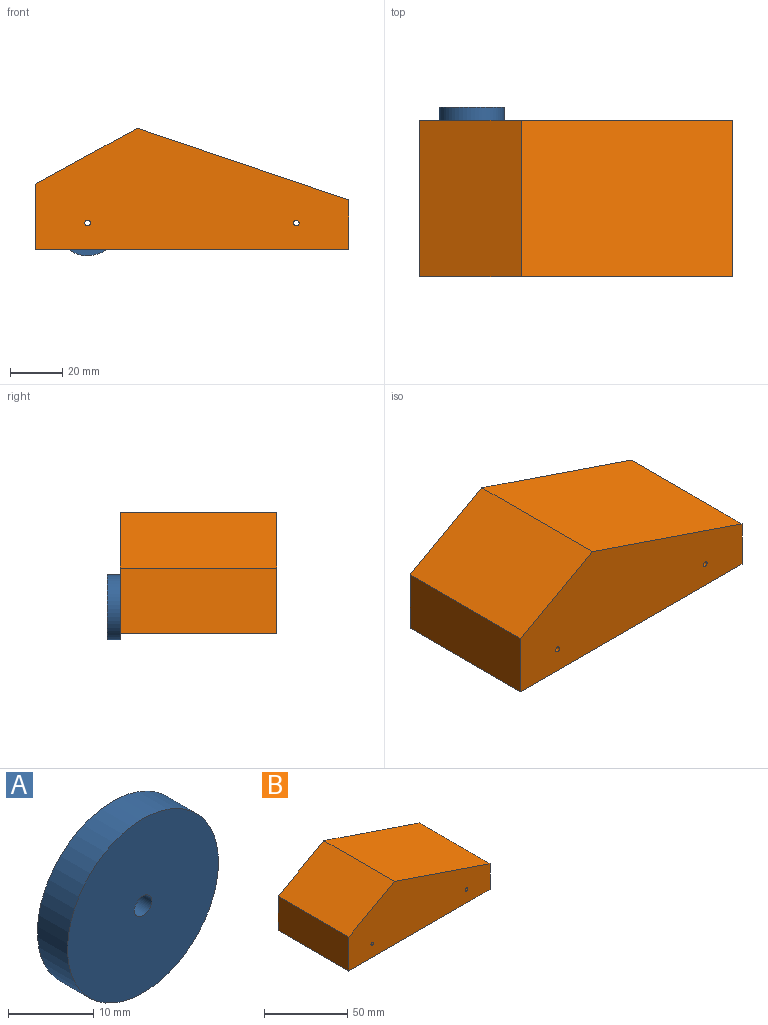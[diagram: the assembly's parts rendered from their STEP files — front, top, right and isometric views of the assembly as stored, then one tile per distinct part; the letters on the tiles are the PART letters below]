
ASSEMBLY  parts=2 mates=1
PART A: 4 faces, bbox 25x5x25 mm
  f0: cylinder r=1.43mm len=5mm, axis (0,1,0), area 44.8mm2, adj f2,f3
  f1: cylinder r=12.5mm len=25mm, axis (0,1,0), area 392.7mm2, adj f2,f3
  f2: plane 25x25mm, normal (0,-1,0), area 484.5mm2, adj f0,f1
  f3: plane 25x25mm, normal (0,1,0), area 484.5mm2, adj f0,f1
PART B: 9 faces, bbox 120x60x46.4 mm
  f0: plane 120x60mm, normal (0,0,-1), area 7200mm2, adj f1,f5,f7,f8
  f1: plane 60x18.92mm, normal (1,0,0), area 1135.1mm2, adj f0,f2,f7,f8
  f2: plane 81x60mm, normal (0.32,0,0.95), area 5131.6mm2, adj f1,f3,f7,f8
  f3: plane 60x39mm, normal (-0.48,0,0.88), area 2668.3mm2, adj f2,f5,f7,f8
  f4: cylinder r=1.07mm len=60mm, axis (0,1,0), area 405.3mm2, adj f7,f8
  f5: plane 60x25mm, normal (-1,0,0), area 1500mm2, adj f0,f3,f7,f8
  f6: cylinder r=1.07mm len=60mm, axis (0,1,0), area 405.3mm2, adj f7,f8
  f7: plane 120x46.37mm, normal (0,-1,0), area 4028.8mm2, adj f0,f1,f2,f3,f4,f5,f6
  f8: plane 120x46.37mm, normal (0,1,0), area 4028.8mm2, adj f0,f1,f2,f3,f4,f5,f6
PLACE A t=(16.19,20.76,-0.51)mm
PLACE B t=(-3.81,15.76,-10.51)mm
MATE fastened B.f6 <-> A.f0  axis (0,1,0) through (16.19,15.76,-0.51)mm
